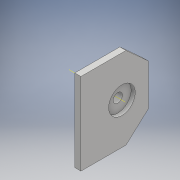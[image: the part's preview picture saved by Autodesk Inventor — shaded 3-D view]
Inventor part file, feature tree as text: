
AUTODESK INVENTOR PART (.ipt)
format: ipt  version: 2017 (Build 210142000, 142)  size: 145,920 bytes
history: native  units: mm
features: extrude x6, sketch x5, projected_geometry x2
ambient origin geometry x8: Origin, YZ Plane, XZ Plane, XY Plane, X Axis, Y Axis, Z Axis, Center Point
bodies: Solide1 (feature_tree)
feature tree (13):
  extrude  "Extrusion1"  Depth=10.5mm
  extrude  "Extrusion2"  Depth=14.0mm
  extrude  "Extrusion7"  Depth=10.0mm TaperAngle=0.0deg
  extrude  "Extrusion10"  Depth=3.0mm TaperAngle=0.0deg
  extrude  "Extrusion11"  Depth=3.0mm
  extrude  "Extrusion12"  Depth=4.5mm
  sketch  "Esquisse1"
  sketch  "Esquisse7"
  sketch  "Esquisse12"
  projected_geometry  "Boucle projetée5"
  sketch  "Esquisse13"
  sketch  "Esquisse14"
  projected_geometry  "Boucle projetée6"
